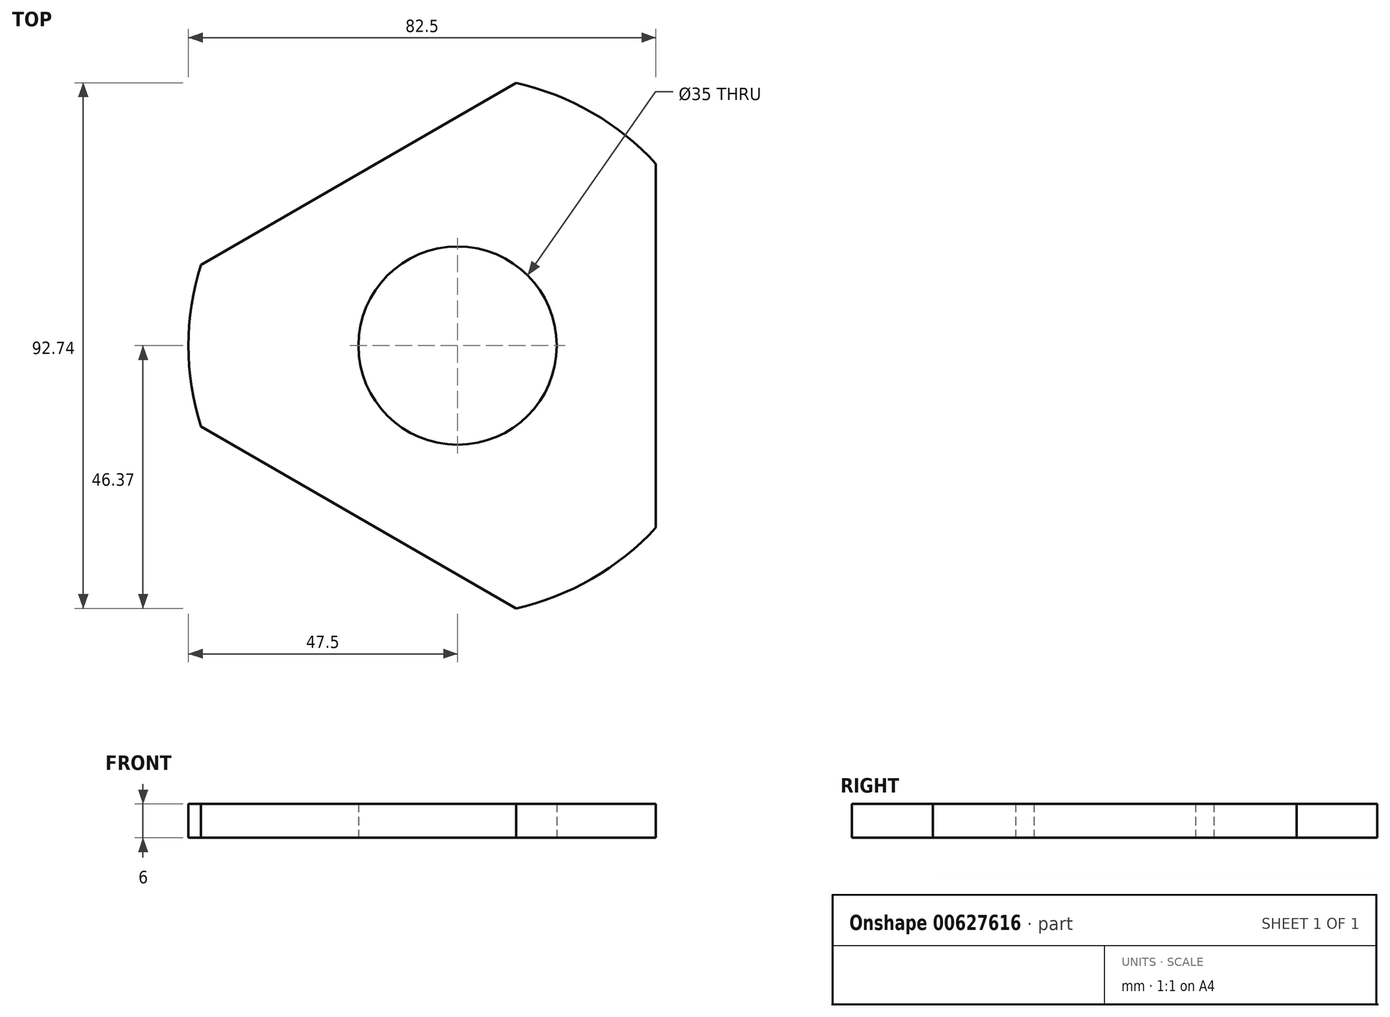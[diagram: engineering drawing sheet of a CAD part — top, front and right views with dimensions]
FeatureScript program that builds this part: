
annotation { "Feature Type Name" : "Feature", "Feature Type Description" : "" }
export const myFeature = defineFeature(function(context is Context, id is Id, definition is map)
    precondition{}
    {
        {
            var Q0;
            Q0=qCreatedBy(makeId("Top.planeOp"),FACE);
            var sketch = newSketch(context, id + "F0", { "sketchPlane" : qUnion([Q0])});
            skArc(sketch, "E0", {"start": v(-45.31, 14.25) * mm, "mid": v(-47.5, 0) * mm, "end": v(-45.31, -14.25) * mm});
            skCircle(sketch, "E1.cCircle", {"center": v(0, 0) * mm, "radius": 35 * mm, "construction": true});
            skLineSegment(sketch, "E1.0", {"start": v(35, 32.11) * mm, "end": v(35, -32.11) * mm});
            skLineSegment(sketch, "E1.1", {"start": v(10.31, -46.37) * mm, "end": v(-45.31, -14.25) * mm});
            skLineSegment(sketch, "E1.2", {"start": v(-45.31, 14.25) * mm, "end": v(10.31, 46.37) * mm});
            skPoint(sketch, "E1.0.midPoint", {"position": v(35, 0) * mm});
            skCircle(sketch, "E2", {"center": v(0, 0) * mm, "radius": 17.5 * mm});
            skPoint(sketch, "E3.orphan", {"position": v(35, 60.62) * mm});
            skArc(sketch, "E4.trimOffspring", {"start": v(35, 32.11) * mm, "mid": v(23.75, 41.14) * mm, "end": v(10.31, 46.37) * mm});
            skPoint(sketch, "E5.orphan", {"position": v(-70, 0) * mm});
            skPoint(sketch, "E6.orphan", {"position": v(35, -60.62) * mm});
            skArc(sketch, "E7.trimOffspring", {"start": v(10.31, -46.37) * mm, "mid": v(23.75, -41.14) * mm, "end": v(35, -32.11) * mm});
            skSolve(sketch);
        }
        {
            var Q0;
            Q0=makeQuery(id+"F0.imprint","IMPRINT",FACE,{"disambiguationData":[TD([[makeQuery(id+"F0.imprint","IMPRINT",EDGE,{"derivedFrom":sQuery(id+"F0.wireOp",EDGE,"E0")}),1.0]])]});
            extrude(context, id + "F1", {"entities" : qUnion([Q0]), "depth" : 6 * mm, "offsetDistance" : 25 * mm});
        }
    });
